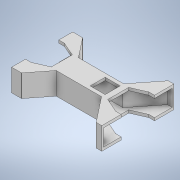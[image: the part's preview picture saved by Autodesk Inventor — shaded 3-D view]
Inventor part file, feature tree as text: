
AUTODESK INVENTOR PART (.ipt)
format: ipt  version: 2022 (Build 260153000, 153)  size: 247,296 bytes
history: native  units: mm
features: extrude x7, sketch x7
ambient origin geometry x8: Origin, YZ Plane, XZ Plane, XY Plane, X Axis, Y Axis, Z Axis, Center Point
bodies: Solid1 (feature_tree)
feature tree (14):
  extrude  "Extrusion1"  Depth=65.0mm
  extrude  "Extrusion2"  Depth=10.0mm
  extrude  "Extrusion3"  Depth=3.0mm
  extrude  "Extrusion4"  Depth=5.0mm TaperAngle=0.0deg
  extrude  "Extrusion5"  Depth=30.0mm
  extrude  "Extrusion6"  Depth=35.4mm
  extrude  "Extrusion7"  Depth=18.0mm
  sketch  "Sketch1"  dims[d0=172.412mm d1=65.0mm]
  sketch  "Sketch2"  dims[d2=65.0mm d7=10.0mm]
  sketch  "Sketch3"  dims[d8=5.0mm d9=0.0mm d10=3.0mm]
  sketch  "Sketch4"  dims[d11=30.0mm d12=0.0mm d13=5.0mm d14=0.0mm]
  sketch  "Sketch5"  dims[d15=30.0mm d16=30.0mm]
  sketch  "Sketch6"  dims[d17=10.0mm d18=35.4mm]
  sketch  "Sketch7"  dims[d19=18.85mm d20=18.85mm d21=0.0mm d22=0.0mm d23=10.0mm d24=10.0mm d25=0.0mm d26=0.0mm d27=3.0mm d28=3.0mm d29=18.0mm d30=0.0mm d33=27.0mm d34=27.0mm d35=18.0mm d36=0.0mm]
